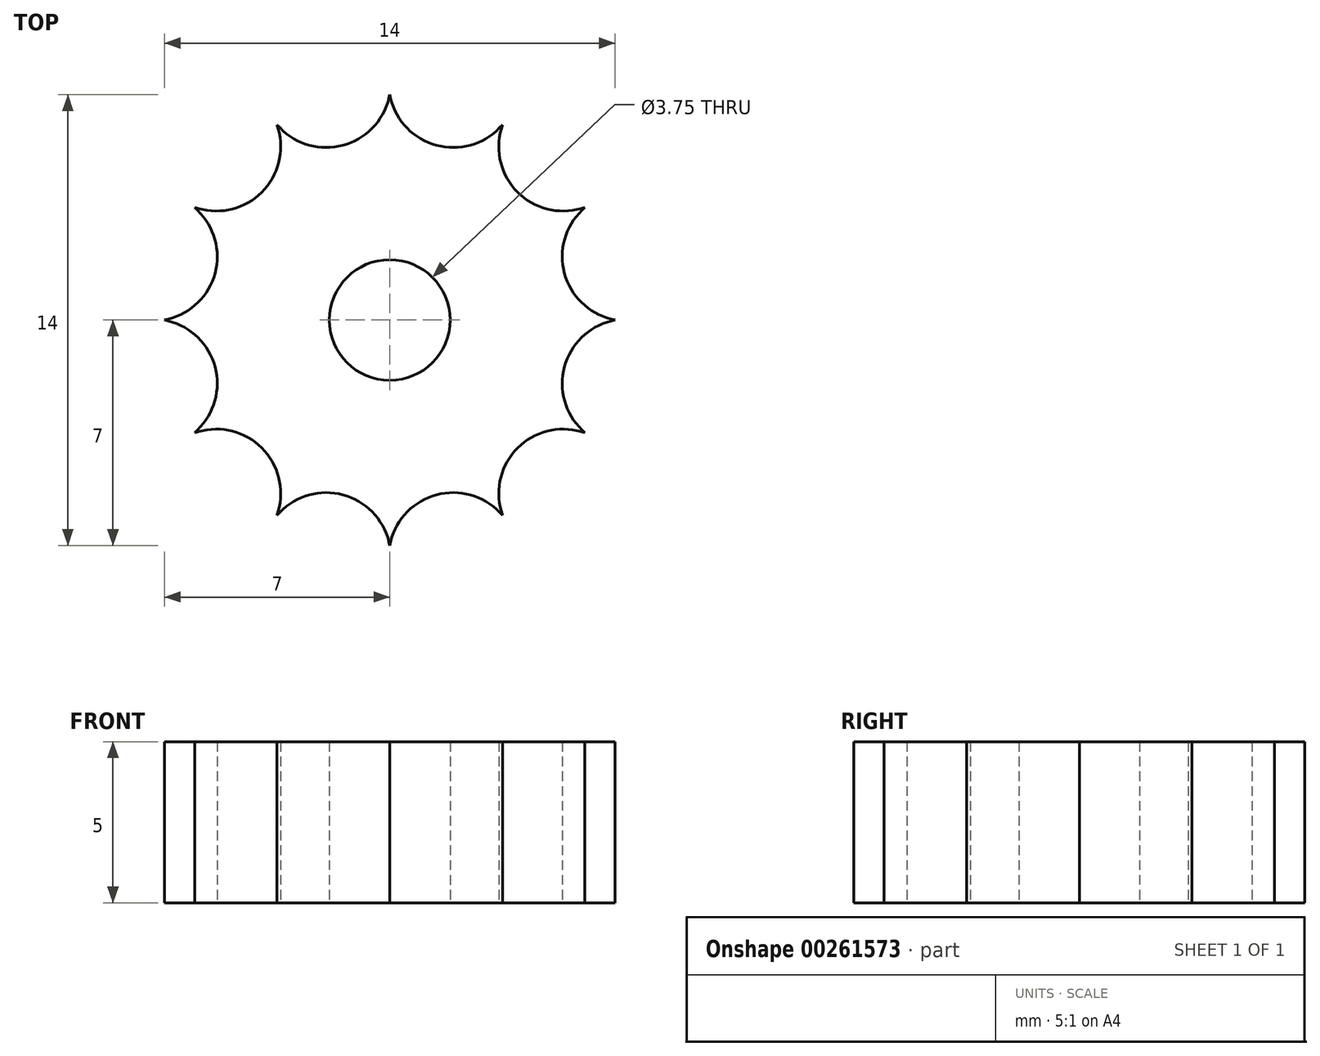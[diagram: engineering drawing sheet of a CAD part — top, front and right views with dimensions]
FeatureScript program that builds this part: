
annotation { "Feature Type Name" : "Feature", "Feature Type Description" : "" }
export const myFeature = defineFeature(function(context is Context, id is Id, definition is map)
    precondition{}
    {
        {
            var Q0;
            Q0=qCreatedBy(makeId("Top.planeOp"),FACE);
            var sketch = newSketch(context, id + "F0", { "sketchPlane" : qUnion([Q0])});
            skCircle(sketch, "E0", {"center": v(0, 0) * mm, "radius": 1.88 * mm});
            skLineSegment(sketch, "E1", {"start": v(-3.5, 6.06) * mm, "end": v(-3.4, 5.97) * mm});
            skLineSegment(sketch, "E2", {"start": v(-0.03, 6.87) * mm, "end": v(0, 7) * mm});
            skPoint(sketch, "E3.end.orphan", {"position": v(-1.81, 6.76) * mm});
            skLineSegment(sketch, "E4.1.0", {"start": v(-6.06, 3.5) * mm, "end": v(-2.47, 2.47) * mm});
            skLineSegment(sketch, "E4.1.1", {"start": v(-2.47, 2.47) * mm, "end": v(-3.5, 6.06) * mm});
            skLineSegment(sketch, "E4.2.0", {"start": v(-7, 0) * mm, "end": v(-3.38, 0.9) * mm});
            skLineSegment(sketch, "E4.2.1", {"start": v(-3.38, 0.9) * mm, "end": v(-6.06, 3.5) * mm});
            skLineSegment(sketch, "E4.3.0", {"start": v(-6.06, -3.5) * mm, "end": v(-3.38, -0.9) * mm});
            skLineSegment(sketch, "E4.3.1", {"start": v(-3.38, -0.9) * mm, "end": v(-7, 0) * mm});
            skLineSegment(sketch, "E4.4.0", {"start": v(-3.5, -6.06) * mm, "end": v(-2.47, -2.47) * mm});
            skLineSegment(sketch, "E4.4.1", {"start": v(-2.47, -2.47) * mm, "end": v(-6.06, -3.5) * mm});
            skLineSegment(sketch, "E4.5.0", {"start": v(0, -7) * mm, "end": v(-0.9, -3.38) * mm});
            skLineSegment(sketch, "E4.5.1", {"start": v(-0.9, -3.38) * mm, "end": v(-3.5, -6.06) * mm});
            skLineSegment(sketch, "E4.6.0", {"start": v(3.5, -6.06) * mm, "end": v(0.9, -3.38) * mm});
            skLineSegment(sketch, "E4.6.1", {"start": v(0.9, -3.38) * mm, "end": v(0, -7) * mm});
            skLineSegment(sketch, "E4.7.0", {"start": v(6.06, -3.5) * mm, "end": v(2.47, -2.47) * mm});
            skLineSegment(sketch, "E4.7.1", {"start": v(2.47, -2.47) * mm, "end": v(3.5, -6.06) * mm});
            skLineSegment(sketch, "E4.8.0", {"start": v(7, 0) * mm, "end": v(3.38, -0.9) * mm});
            skLineSegment(sketch, "E4.8.1", {"start": v(3.38, -0.9) * mm, "end": v(6.06, -3.5) * mm});
            skLineSegment(sketch, "E4.9.0", {"start": v(6.06, 3.5) * mm, "end": v(3.38, 0.9) * mm});
            skLineSegment(sketch, "E4.9.1", {"start": v(3.38, 0.9) * mm, "end": v(7, 0) * mm});
            skLineSegment(sketch, "E4.10.0", {"start": v(3.5, 6.06) * mm, "end": v(2.47, 2.47) * mm});
            skLineSegment(sketch, "E4.10.1", {"start": v(2.47, 2.47) * mm, "end": v(6.06, 3.5) * mm});
            skLineSegment(sketch, "E4.11.0", {"start": v(0, 7) * mm, "end": v(0.9, 3.38) * mm});
            skLineSegment(sketch, "E4.11.1", {"start": v(0.9, 3.38) * mm, "end": v(3.5, 6.06) * mm});
            skPoint(sketch, "E5.visualSharp", {"position": v(-0.9, 3.38) * mm});
            skArc(sketch, "E5.filletArc", {"start": v(-3.4, 5.97) * mm, "mid": v(-1.45, 5.43) * mm, "end": v(-0.03, 6.87) * mm});
            skArc(sketch, "E6.1.0", {"start": v(-5.94, 3.46) * mm, "mid": v(-3.97, 3.97) * mm, "end": v(-3.46, 5.94) * mm});
            skArc(sketch, "E6.2.0", {"start": v(-6.87, 0.03) * mm, "mid": v(-5.43, 1.45) * mm, "end": v(-5.97, 3.4) * mm});
            skArc(sketch, "E6.3.0", {"start": v(-5.97, -3.4) * mm, "mid": v(-5.43, -1.45) * mm, "end": v(-6.87, -0.03) * mm});
            skArc(sketch, "E6.4.0", {"start": v(-3.46, -5.94) * mm, "mid": v(-3.97, -3.97) * mm, "end": v(-5.94, -3.46) * mm});
            skArc(sketch, "E6.5.0", {"start": v(-0.03, -6.87) * mm, "mid": v(-1.45, -5.43) * mm, "end": v(-3.4, -5.97) * mm});
            skArc(sketch, "E6.6.0", {"start": v(3.4, -5.97) * mm, "mid": v(1.45, -5.43) * mm, "end": v(0.03, -6.87) * mm});
            skArc(sketch, "E6.7.0", {"start": v(5.94, -3.46) * mm, "mid": v(3.97, -3.97) * mm, "end": v(3.46, -5.94) * mm});
            skArc(sketch, "E6.8.0", {"start": v(6.87, -0.03) * mm, "mid": v(5.43, -1.45) * mm, "end": v(5.97, -3.4) * mm});
            skArc(sketch, "E6.9.0", {"start": v(5.97, 3.4) * mm, "mid": v(5.43, 1.45) * mm, "end": v(6.87, 0.03) * mm});
            skArc(sketch, "E6.10.0", {"start": v(3.46, 5.94) * mm, "mid": v(3.97, 3.97) * mm, "end": v(5.94, 3.46) * mm});
            skArc(sketch, "E6.11.0", {"start": v(0.03, 6.87) * mm, "mid": v(1.45, 5.43) * mm, "end": v(3.4, 5.97) * mm});
            skSolve(sketch);
        }
        {
            var Q0;
            Q0 = qSketchRegion(id + "F0", true);
            extrude(context, id + "F1", {"entities" : qUnion([Q0]), "depth" : 5 * mm});
        }
    });
